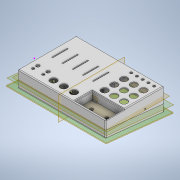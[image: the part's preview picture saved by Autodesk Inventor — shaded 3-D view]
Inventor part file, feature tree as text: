
AUTODESK INVENTOR PART (.ipt)
format: ipt  version: 2020 (Build 240168000, 168)  size: 2,439,680 bytes
history: native  units: mm
features: extrude x42, sketch x31, plane x30, projected_geometry x11, split x10, loft x4, fillet x3, other x3, boolean_combine x3, chamfer x1, mirror x1
ambient origin geometry x8: Origin, YZ Plane, XZ Plane, XY Plane, X Axis, Y Axis, Z Axis, Center Point
bodies: Solid3 (feature_tree), Solid4 (feature_tree), Solid5 (feature_tree), Solid6 (feature_tree), Solid7 (feature_tree), Solid8 (feature_tree), Solid9 (feature_tree), Solid10 (feature_tree), Solid11 (feature_tree), Solid12 (feature_tree), Solid13 (feature_tree), Solid14 (feature_tree), Solid15 (feature_tree), Solid16 (feature_tree), Solid17 (feature_tree), Solid18 (feature_tree), Solid19 (feature_tree), Solid20 (feature_tree), Solid21 (feature_tree), Solid24 (feature_tree), Solid25 (feature_tree)
feature tree (139):
  sketch  "Sketch2"  dims[d19=6.3mm d21=16.5mm]
  sketch  "Sketch3"  dims[d28=12.0mm d31=14.0mm d39=12.0mm d40=9.75mm]
  plane  "Work Plane1"
  extrude  "Extrusion7"  Depth=16.5mm
  extrude  "Extrusion10"  Depth=14.0mm
  fillet  "Fillet3"  Radius=12.0mm
  fillet  "Fillet5"  Radius=9.75mm
  plane  "Work Plane2"
  plane  "Work Plane3"
  other  "slidermount"
  sketch  "Sketch16"  dims[d41=23.75mm d42=23.75mm]
  extrude  "Extrusion17"  Depth=23.75mm
  extrude  "Extrusion18"  Depth=8.37mm
  sketch  "Sketch20"  dims[d66=5.8mm d87=25.0mm]
  sketch  "Sketch19"  dims[d46=23.75mm d64=8.37mm]
  loft  "Loft1"
  loft  "Loft2"
  extrude  "Extrusion19"  Depth=25.0mm
  extrude  "Extrusion20"  Depth=40.0mm
  fillet  "Fillet8"  Radius=40.0mm
  extrude  "Extrusion21"  Depth=102.595604mm
  other  "slidercase"
  extrude  "Extrusion23"  Depth=75.999999mm
  other  "slidercaseholders"
  extrude  "part2wall"  Depth=1.25mm
  extrude  "Extrusion25"  Depth=1.25mm
  extrude  "part2main"  Depth=1.25mm
  extrude  "Extrusion27"  Depth=2.5mm
  extrude  "Extrusion28"  Depth=2.5mm
  sketch  "Sketch31"  dims[d93=3.52mm d109=40.0mm d110=40.0mm]
  extrude  "Extrusion30"  Depth=2.0mm TaperAngle=0.0deg
  extrude  "Extrusion31"  Depth=2.0mm
  extrude  "Extrusion32"  Depth=2.0mm
  plane  "Work Plane5"
  plane  "Work Plane6"
  sketch  "Sketch35"  dims[d129=5.0mm d131=75.999999mm]
  plane  "Work Plane7"
  extrude  "Extrusion36"  Depth=14.0mm
  extrude  "Extrusion37"  Depth=6.0mm
  plane  "Work Plane8"
  plane  "Work Plane10"
  extrude  "Extrusion40"  Depth=20.0mm TaperAngle=0.0deg
  sketch  "Sketch43"  dims[d132=1.25mm d133=1.25mm]
  sketch  "Sketch45"  dims[d134=1.25mm d135=1.25mm]
  extrude  "Extrusion41"  Depth=2.0mm
  extrude  "Extrusion42"  TaperAngle=0.0deg  [1 undecoded]
  extrude  "Extrusion43"  TaperAngle=0.0deg  [1 undecoded]
  extrude  "Extrusion44"  TaperAngle=0.0deg  [1 undecoded]
  extrude  "Extrusion45"  Depth=2.0mm
  plane  "Work Plane11"
  plane  "Work Plane12"
  plane  "Work Plane13"
  plane  "Work Plane14"
  plane  "Work Plane15"
  split  "Split1"
  split  "Split2"
  split  "Split3"
  split  "Split4"
  split  "Split5"
  boolean_combine  "Combine1"
  plane  "Work Plane17"
  sketch  "Sketch48"  dims[d140=2.5mm d141=2.5mm]
  extrude  "Extrusion46"  Depth=4.0mm
  extrude  "Extrusion47"  Depth=2.0mm
  extrude  "Extrusion48"  Depth=1.0mm
  extrude  "Extrusion50"  Depth=2.0mm
  plane  "Work Plane18"
  plane  "Work Plane19"
  plane  "Work Plane20"
  plane  "Work Plane21"
  split  "Split6"
  split  "Split7"
  split  "Split8"
  split  "Split9"
  boolean_combine  "Combine2"
  extrude  "Extrusion51"  Depth=2.0mm
  extrude  "Extrusion52"  Depth=2.0mm
  extrude  "Extrusion53"  Depth=2.0mm
  extrude  "Extrusion58"  Depth=1.0mm TaperAngle=0.0deg
  plane  "Work Plane23"
  boolean_combine  "Combine3"
  extrude  "Extrusion62"  Depth=1.0mm TaperAngle=0.0deg
  plane  "Work Plane24"
  sketch  "Sketch59"  dims[d187=14.0mm d188=6.0mm]
  extrude  "Extrusion63"  Depth=6.4mm
  extrude  "Extrusion64"  Depth=10.6mm
  plane  "Work Plane25"
  plane  "Work Plane26"
  extrude  "Extrusion65"  Depth=1.0mm
  plane  "Work Plane27"
  extrude  "Extrusion66"  Depth=2.0mm TaperAngle=0.0deg
  plane  "Work Plane28"
  sketch  "Sketch65"  dims[d202=0.0mm d203=90.0deg d204=0.0mm d205=0.0mm]
  plane  "Work Plane29"
  sketch  "Sketch66"  dims[d206=10.0mm d207=0.0mm d208=2.0mm]
  loft  "Loft3"
  loft  "Loft4"
  split  "Split11"
  sketch  "Sketch67"  dims[d212=4.0mm d213=4.0mm]
  extrude  "Extrusion67"  Depth=0.1mm
  extrude  "Extrusion68"  Depth=80.1mm TaperAngle=0.0deg
  chamfer  "Chamfer4"  Distance=0.5mm
  extrude  "Extrusion69"  Depth=0.5mm
  plane  "Work Plane31"
  mirror  "Mirror1"
  extrude  "Extrusion70"  Depth=35.0mm TaperAngle=0.0deg
  plane  "Work Plane32"
  extrude  "Extrusion71"  Depth=3.0mm
  projected_geometry  "Projected Loop1"
  sketch  "Sketch23"  dims[d88=25.0mm d89=25.0mm]
  sketch  "Sketch25"  dims[d90=25.0mm d91=25.0mm]
  projected_geometry  "Projected Loop2"
  projected_geometry  "Projected Loop3"
  sketch  "Sketch33"  dims[d114=20.0mm d116=102.595604mm]
  plane  "Work Plane4"
  plane  "Work Plane9"
  projected_geometry  "Projected Loop5"
  projected_geometry  "Projected Loop6"
  projected_geometry  "Projected Loop7"
  projected_geometry  "Projected Loop8"
  sketch  "Sketch46"  dims[d136=1.25mm d137=1.25mm]
  projected_geometry  "Projected Loop9"
  sketch  "Sketch47"  dims[d138=2.5mm d139=2.5mm]
  plane  "Work Plane16"
  sketch  "Sketch50"  dims[d142=2.0mm d143=0.0mm d153=2.0mm d154=0.0mm]
  sketch  "Sketch52"  dims[d155=2.0mm d160=2.0mm]
  projected_geometry  "Projected Loop10"
  projected_geometry  "Projected Loop11"
  sketch  "Sketch54"  dims[d161=2.0mm d162=2.0mm]
  sketch  "Sketch58"  dims[d163=1.5mm d186=14.0mm]
  sketch  "Sketch60"  dims[d189=35.0mm d190=0.0mm d191=20.0mm d192=0.0mm]
  sketch  "Sketch61"  dims[d193=2.0mm d194=2.0mm]
  sketch  "Sketch63"  dims[d195=2.0mm d196=0.0mm d197=90.0deg]
  sketch  "Sketch64"  dims[d198=0.0mm d199=90.0deg d200=0.0mm d201=90.0deg]
  sketch  "Sketch68"  dims[d214=3.0mm d215=0.0mm d217=2.0mm]
  sketch  "Sketch69"  dims[d223=1.0mm d224=1.0mm]
  sketch  "Sketch70"  dims[d225=1.0mm d226=0.0mm d228=2.0mm]
  sketch  "Sketch71"  dims[d230=0.1mm d231=2.0mm d234=2.0mm d237=2.0mm d238=1.0mm d239=0.0mm d240=1.0mm d241=0.0mm d242=6.4mm d243=10.6mm d244=1.0mm d245=2.0mm d246=0.0mm d247=0.1mm d248=0.1mm d249=0.1mm d250=80.1mm d251=0.0mm d252=0.5mm d253=0.5mm d254=35.0mm d255=0.0mm d257=3.0mm d258=3.0mm d259=3.0mm d260=3.0mm d261=3.0mm d264=10.0mm d265=0.0mm d266=10.0mm d267=0.0mm d268=4.0mm d269=3.0mm d272=13.0mm d273=10.0mm d274=0.0mm d275=1.6mm d289=2.1mm d290=4.85mm d291=4.2mm d292=4.85mm d293=4.2mm d294=4.85mm d295=4.2mm d296=4.85mm d297=4.2mm d298=4.85mm d299=4.2mm d300=4.85mm d301=4.2mm d302=4.85mm d303=4.2mm d304=1.5mm d305=4.0mm d306=4.0mm d307=4.0mm d308=3.0mm d309=2.0mm d310=3.0mm d311=3.0mm d312=3.0mm d313=3.0mm d314=3.0mm d315=2.0mm d316=0.0mm d317=2.6mm d318=0.0mm d322=34.25mm d323=10.0mm d326=7.0mm d327=0.0mm d328=3.0mm d329=3.0mm d330=3.0mm d331=3.0mm d332=3.0mm d333=3.0mm d334=10.0mm d335=0.0mm d336=10.0mm d337=0.0mm d338=10.0mm d339=0.0mm d340=10.0mm d341=0.0mm d342=8.5mm d343=8.5mm d344=10.0mm d345=0.0mm d347=-23.5mm d348=2.7mm d365=8.5mm d366=8.5mm d367=10.0mm d368=0.0mm d369=2.0mm d370=0.0mm d371=0.0mm d372=0.0mm d375=2.0mm d376=0.0mm d377=6.5mm d378=4.0mm d379=4.0mm d380=4.0mm d381=4.0mm d382=4.0mm d383=2.0mm d384=0.0mm d385=5.5mm d386=5.5mm d387=3.0mm d388=3.0mm d389=2.0mm d390=0.0mm d391=23.0mm d392=5.9mm d393=0.0mm d406=5.6mm d408=5.6mm d409=1.2mm d410=0.0mm d419=12.0mm d420=12.0mm d457=10.0mm d458=0.0mm d459=10.0mm d460=0.0mm d461=10.0mm d462=0.0mm d463=15.0mm d464=-35.0mm d465=17.0mm d466=0.0mm d467=-22.0mm d468=17.0mm d469=0.0mm d470=2.0mm d471=0.0mm d472=90.0deg d473=0.0mm d474=90.0deg d475=0.0mm d476=90.0deg d477=0.0mm d478=90.0deg d479=45.0mm d480=7.0mm d481=3.4mm d485=27.0mm d486=0.0mm d487=4.0mm d488=0.0mm d489=6.0mm d490=2.0mm d491=45.0deg d492=0.1mm d493=21.75mm d494=0.0mm d495=9.0mm d496=0.0mm d497=2.0mm d498=9.0mm d499=0.0mm d94=0.5mm d95=0.872665mm d96=0.5mm d97=0.872665mm d102=0.5mm d103=0.872665mm d104=0.5mm d105=0.872665mm d122=0.5mm d123=0.872665mm d124=0.5mm d125=0.872665mm d144=0.5mm d145=0.872665mm d149=0.5mm d150=0.872665mm d151=0.5mm d152=0.872665mm d168=0.5mm d169=0.872665mm d170=0.5mm d171=0.872665mm d172=0.872665mm d173=0.5mm d174=0.872665mm d175=0.5mm d176=0.872665mm d184=0.5mm d185=0.872665mm d220=0.5mm d221=0.872665mm d222=0.5mm d319=0.5mm d320=0.872665mm d321=0.5mm d346=0.5mm d349=0.872665mm d437=0.5mm d438=0.872665mm d439=0.5mm d440=0.872665mm d482=0.5mm d483=0.872665mm d484=0.5mm]
  projected_geometry  "Project Cut Edges1"
note: 3 required parameter values undecoded (feature->parameter linkage not recoverable at this tier; creation-order binding heuristic only, values carry confidence <= 0.55)
